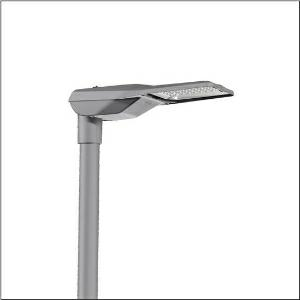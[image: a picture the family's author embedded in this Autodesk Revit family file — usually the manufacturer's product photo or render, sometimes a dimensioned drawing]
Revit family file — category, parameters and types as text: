
# Revit family: streetlight_sl_21_iq_mini___p0_8a_5xe2u31v08gb_4f31
name_source: partatom
category: Lighting Fixtures
units: mm (PartAtom-declared; Revit-internal decimal feet)

## family parameters
Cut with Voids When Loaded = No
Host = Face
Light Source = No
Part Type = Normal
Room Calculation Point = No
Round Connector Dimension = Use Diameter
Shared = No

## types (1)
- --- (1 x LED, 6040 lm, 39.8 W, 3000K)
    Apparent Load = 40 VA
    CIE Flux Codes = 33 69 96 100 100
    Color Rendering = 70
    Color Temperature = 3000K
    Default Elevation = 1800 mm
    Description = Streetlight SL 21 iQ mini, mast luminaire, primary light control with lens, of PMMA, primary optical cover: cover, of toughened safety glass, transparent, light distribution: P0.8a, light emission: direct distribution, primary light characteristic: asymmetric, installation type: post-top, side-entry, LED, High Power LED, rated luminous flux: 6.040lm, luminous efficacy: 152lm/W, light colour: 730, colour temperature: 3000K, control gear: iQ-Street Remote, D4i with power reduction, control: pre-setting: logarithmic dimming characteristic, Street-Remote, Auto-Match, Temp-Guard, Lumen-Switch, Night-Set, Smart-Wire, Light-Fading, Desk-Remote (wireless, voltage-free reading and setting of iQ features in the workshop via application-optimized NFC function/RFID function), optimised constant luminous flux control (CLO 2.0), mains connection: 220..240V, AC, 50/60Hz, start of lifetime: 40W, end of service life: 41W, reduction: 18W, luminaire housing, of diecast aluminium, powder-coated, SITECO metallic grey (DB 702S), corrosivity category C5 high according to DIN EN ISO 12944, please order mast flange separately, inclination adjustable: 0°, 5°, 10°, 15°, sealing non-destructively replaceable, multi-level sealing system, length: 628mm, width: 235mm, height: 110mm, mast flange for spigot size: 42mm (side-entry): 5XC10008XM4, 60/48mm (side-entry/post-top): 5XC10108XM2, 76/60mm (side-entry/post-top): 5XC10108XM1, mounting height: 4..8m, Smart Interface above, protection rating (complete): IP66, insulation class (complete): insulation class II (safety insulation), certification: CE, ENEC, ENEC+, VDE, impact resistance: IK10, permissible operating ambient temperature for outdoor applications: -40..+50°C, standard-compliant lighting for roads and squares, packaging unit: 1 piece

Light Distribution: P0.8a
    Height = 110 mm
    Lamp = 1 x LED
    Lamp Light Flux = 6040 lm
    Lamp Power = 39.8 W
    Lamp count = 1
    Length = 625 mm
    Luminous efficacy = 152 lm/W
    Manufacturer = Siteco
    ModVariant = No
    Model = 5XE2U31V08GB
    Number of Poles = 1
    OnlyDefault = Yes
    Power Factor = 1
    Product Name = Streetlight SL 21 iQ mini | P0.8a
    Product group = mast luminaire | pylon top
    ProductGroupID = 6100
    Protection Class = Protection class II
    Protection Degree = IP 66
    RLX_Detail_Level = 1
    RLX_Emergency_Light_Flux = 0 lm
    RLX_Emergency_Type = 0
    RLX_Emergency_Type_DB = No
    RlxData = <blob elided: 92373 chars, md5=205663b9>
    Socket = socket
    Standby Power = 0 W
    System Light Flux = 6040 lm
    System Power = 40 W
    Type Comments = factory setting: luminous flux: 100 % | dim-lin: 254 | 800 mA
    Type Image = l_1003515.jpg
    URL = http://relux.com
    VarID = @adj_081879
    Voltage = 0 V
    Weight = 0.00 kg
    Width = 234 mm

## geometry (parser evidence)
native form markers: Blend x4, Sweep x12
no freeform markers — native parametric forms only
